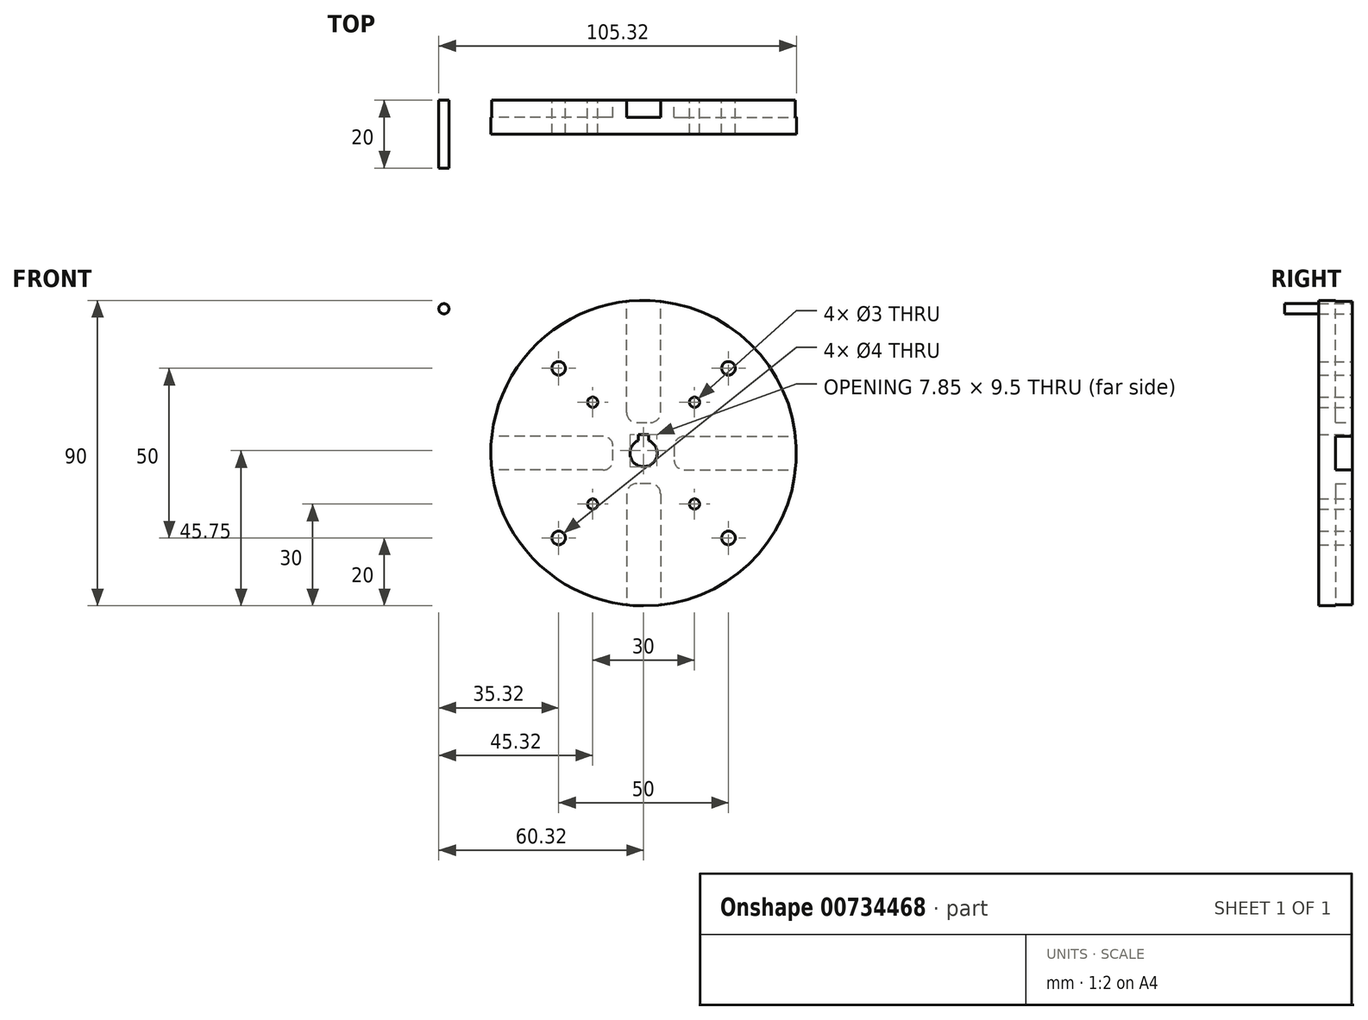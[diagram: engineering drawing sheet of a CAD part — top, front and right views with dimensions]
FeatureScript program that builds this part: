
annotation { "Feature Type Name" : "Feature", "Feature Type Description" : "" }
export const myFeature = defineFeature(function(context is Context, id is Id, definition is map)
    precondition{}
    {
        {
            var Q0;
            Q0=qCreatedBy(makeId("Front.planeOp"),FACE);
            var sketch = newSketch(context, id + "F0", { "sketchPlane" : qUnion([Q0])});
            skCircle(sketch, "E0", {"center": v(0, 0) * mm, "radius": 45 * mm});
            skLineSegment(sketch, "E1", {"start": v(0, 54.43) * mm, "end": v(0, -47.25) * mm, "construction": true});
            skLineSegment(sketch, "E2", {"start": v(-48.85, 0) * mm, "end": v(49.22, 0) * mm, "construction": true});
            skArc(sketch, "E3", {"start": v(-1.5, 3.7) * mm, "mid": v(0, -4) * mm, "end": v(1.5, 3.7) * mm});
            skLineSegment(sketch, "E4", {"start": v(-7.07, 4) * mm, "end": v(7.01, 4) * mm, "construction": true});
            skLineSegment(sketch, "E5.bottom", {"start": v(-1.5, 5.5) * mm, "end": v(1.5, 5.5) * mm});
            skLineSegment(sketch, "E5.left", {"start": v(-1.5, 5.5) * mm, "end": v(-1.5, 3.7) * mm});
            skLineSegment(sketch, "E5.right", {"start": v(1.5, 5.5) * mm, "end": v(1.5, 3.7) * mm});
            skLineSegment(sketch, "E6", {"start": v(38.03, -38.03) * mm, "end": v(-35.78, 35.78) * mm, "construction": true});
            skCircle(sketch, "E7", {"center": v(-15, 15) * mm, "radius": 1.5 * mm});
            skCircle(sketch, "E8.1.0", {"center": v(-15, -15) * mm, "radius": 1.5 * mm});
            skCircle(sketch, "E8.2.0", {"center": v(15, -15) * mm, "radius": 1.5 * mm});
            skCircle(sketch, "E8.3.0", {"center": v(15, 15) * mm, "radius": 1.5 * mm});
            skCircle(sketch, "E9", {"center": v(-25, 25) * mm, "radius": 2 * mm});
            skCircle(sketch, "E10.1.1", {"center": v(-25, -25) * mm, "radius": 2 * mm});
            skCircle(sketch, "E10.2.1", {"center": v(25, -25) * mm, "radius": 2 * mm});
            skCircle(sketch, "E10.3.1", {"center": v(25, 25) * mm, "radius": 2 * mm});
            skSolve(sketch);
        }
        {
            var Q0;
            Q0 = qSketchRegion(id + "F0", true);
            extrude(context, id + "F1", {"entities" : qUnion([Q0]), "depth" : 10 * mm, "offsetDistance" : 25 * mm});
        }
        {
            var Q0;
            Q0=qCreatedBy(makeId("Front.planeOp"),FACE);
            var sketch = newSketch(context, id + "F2", { "sketchPlane" : qUnion([Q0])});
            skLineSegment(sketch, "E11.bottom", {"start": v(12, 5) * mm, "end": v(45, 5) * mm});
            skLineSegment(sketch, "E11.top", {"start": v(12, -5) * mm, "end": v(45, -5) * mm});
            skLineSegment(sketch, "E11.left", {"start": v(9, 2) * mm, "end": v(9, -2) * mm});
            skLineSegment(sketch, "E11.right", {"start": v(45, 5) * mm, "end": v(45, -5) * mm});
            skPoint(sketch, "E12.center", {"position": v(0, 0) * mm});
            skPoint(sketch, "E13.visualSharp", {"position": v(9, 5) * mm});
            skArc(sketch, "E13.filletArc", {"start": v(12, 5) * mm, "mid": v(9.88, 4.12) * mm, "end": v(9, 2) * mm});
            skPoint(sketch, "E14.visualSharp", {"position": v(9, -5) * mm});
            skArc(sketch, "E14.filletArc", {"start": v(9, -2) * mm, "mid": v(9.88, -4.12) * mm, "end": v(12, -5) * mm});
            skLineSegment(sketch, "E15.1.0", {"start": v(-5, 12) * mm, "end": v(-5, 45) * mm});
            skLineSegment(sketch, "E15.1.1", {"start": v(-5, 45) * mm, "end": v(5, 45) * mm});
            skLineSegment(sketch, "E15.1.2", {"start": v(5, 12) * mm, "end": v(5, 45) * mm});
            skArc(sketch, "E15.1.3", {"start": v(2, 9) * mm, "mid": v(4.12, 9.88) * mm, "end": v(5, 12) * mm});
            skLineSegment(sketch, "E15.1.4", {"start": v(-2, 9) * mm, "end": v(2, 9) * mm});
            skArc(sketch, "E15.1.5", {"start": v(-5, 12) * mm, "mid": v(-4.12, 9.88) * mm, "end": v(-2, 9) * mm});
            skLineSegment(sketch, "E15.2.0", {"start": v(-12, -5) * mm, "end": v(-45, -5) * mm});
            skLineSegment(sketch, "E15.2.1", {"start": v(-45, -5) * mm, "end": v(-45, 5) * mm});
            skLineSegment(sketch, "E15.2.2", {"start": v(-12, 5) * mm, "end": v(-45, 5) * mm});
            skArc(sketch, "E15.2.3", {"start": v(-9, 2) * mm, "mid": v(-9.88, 4.12) * mm, "end": v(-12, 5) * mm});
            skLineSegment(sketch, "E15.2.4", {"start": v(-9, -2) * mm, "end": v(-9, 2) * mm});
            skArc(sketch, "E15.2.5", {"start": v(-12, -5) * mm, "mid": v(-9.88, -4.12) * mm, "end": v(-9, -2) * mm});
            skLineSegment(sketch, "E15.3.0", {"start": v(5, -12) * mm, "end": v(5, -45) * mm});
            skLineSegment(sketch, "E15.3.1", {"start": v(5, -45) * mm, "end": v(-5, -45) * mm});
            skLineSegment(sketch, "E15.3.2", {"start": v(-5, -12) * mm, "end": v(-5, -45) * mm});
            skArc(sketch, "E15.3.3", {"start": v(-2, -9) * mm, "mid": v(-4.12, -9.88) * mm, "end": v(-5, -12) * mm});
            skLineSegment(sketch, "E15.3.4", {"start": v(2, -9) * mm, "end": v(-2, -9) * mm});
            skArc(sketch, "E15.3.5", {"start": v(5, -12) * mm, "mid": v(4.12, -9.88) * mm, "end": v(2, -9) * mm});
            skSolve(sketch);
        }
        {
            var Q0;
            Q0 = qSketchRegion(id + "F2", true);
            extrude(context, id + "F3", {"entities" : qUnion([Q0]), "operationType" : NewBodyOperationType.REMOVE, "oppositeDirection" : true, "depth" : -5 * mm, "offsetDistance" : 25 * mm});
        }
        {
            var Q0;
            Q0=qCreatedBy(makeId("Front.planeOp"),FACE);
            var sketch = newSketch(context, id + "F4", { "sketchPlane" : qUnion([Q0])});
            skCircle(sketch, "E16", {"center": v(-58.82, 42.54) * mm, "radius": 1.5 * mm});
            skSolve(sketch);
        }
        {
            var Q0;
            Q0 = qSketchRegion(id + "F4", true);
            extrude(context, id + "F5", {"entities" : qUnion([Q0]), "depth" : 20 * mm, "offsetDistance" : 25 * mm});
        }
    });
